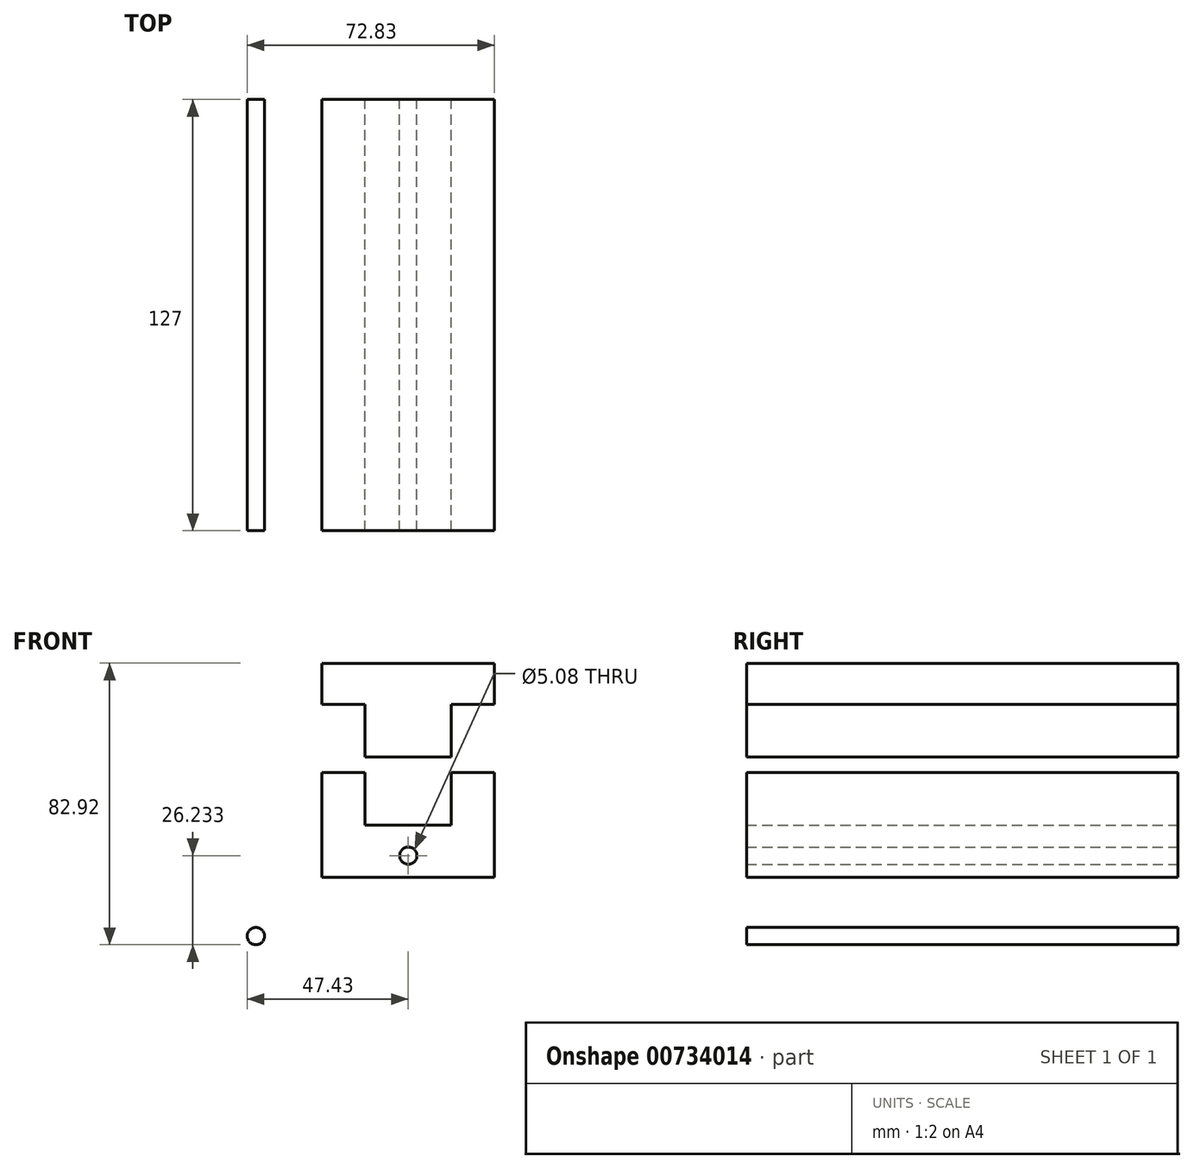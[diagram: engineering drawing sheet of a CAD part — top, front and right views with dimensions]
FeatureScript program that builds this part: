
annotation { "Feature Type Name" : "Feature", "Feature Type Description" : "" }
export const myFeature = defineFeature(function(context is Context, id is Id, definition is map)
    precondition{}
    {
        {
            var Q0;
            Q0=qCreatedBy(makeId("Front.planeOp"),FACE);
            var sketch = newSketch(context, id + "F0", { "sketchPlane" : qUnion([Q0])});
            skLineSegment(sketch, "E0.bottom", {"start": v(-25.4, -15.45) * mm, "end": v(25.4, -15.45) * mm});
            skLineSegment(sketch, "E0.top", {"start": v(-25.4, 15.45) * mm, "end": v(25.4, 15.45) * mm});
            skLineSegment(sketch, "E0.left", {"start": v(-25.4, -15.45) * mm, "end": v(-25.4, 15.45) * mm});
            skLineSegment(sketch, "E0.right", {"start": v(25.4, -15.45) * mm, "end": v(25.4, 15.45) * mm});
            skPoint(sketch, "E0.middle", {"position": v(0, 0) * mm});
            skLineSegment(sketch, "E1", {"start": v(-12.7, 15.45) * mm, "end": v(-12.7, 0) * mm});
            skLineSegment(sketch, "E2", {"start": v(-12.7, 0) * mm, "end": v(12.7, 0) * mm});
            skLineSegment(sketch, "E3", {"start": v(12.7, 0) * mm, "end": v(12.7, 15.45) * mm});
            skCircle(sketch, "E4", {"center": v(0, -9.03) * mm, "radius": 2.54 * mm});
            skSolve(sketch);
        }
        {
            var Q0;
            Q0=makeQuery(id+"F0.imprint","IMPRINT",FACE,{"disambiguationData":[TD([[makeQuery(id+"F0.imprint","IMPRINT",EDGE,{"derivedFrom":sQuery(id+"F0.wireOp",EDGE,"E0.bottom")}),1.0]])]});
            extrude(context, id + "F1", {"entities" : qUnion([Q0]), "endBound" : BoundingType.SYMMETRIC, "depth" : 127 * mm, "offsetDistance" : 25.4 * mm});
        }
        {
            var Q0;
            Q0=qCreatedBy(makeId("Front.planeOp"),FACE);
            var sketch = newSketch(context, id + "F2", { "sketchPlane" : qUnion([Q0])});
            skLineSegment(sketch, "E5.bottom", {"start": v(-12.7, 20.04) * mm, "end": v(12.7, 20.04) * mm});
            skLineSegment(sketch, "E5.top", {"start": v(-12.7, 44.5) * mm, "end": v(12.7, 44.5) * mm});
            skLineSegment(sketch, "E5.left", {"start": v(-12.7, 20.04) * mm, "end": v(-12.7, 44.5) * mm});
            skLineSegment(sketch, "E5.right", {"start": v(12.7, 20.04) * mm, "end": v(12.7, 44.5) * mm});
            skPoint(sketch, "E5.middle", {"position": v(0, 32.27) * mm});
            skLineSegment(sketch, "E6.bottom", {"start": v(-25.4, 35.49) * mm, "end": v(25.4, 35.49) * mm});
            skLineSegment(sketch, "E6.top", {"start": v(-25.4, 47.66) * mm, "end": v(25.4, 47.66) * mm});
            skLineSegment(sketch, "E6.left", {"start": v(-25.4, 35.49) * mm, "end": v(-25.4, 47.66) * mm});
            skLineSegment(sketch, "E6.right", {"start": v(25.4, 35.49) * mm, "end": v(25.4, 47.66) * mm});
            skPoint(sketch, "E6.middle", {"position": v(0, 41.57) * mm});
            skSolve(sketch);
        }
        {
            var Q0;
            Q0 = qSketchRegion(id + "F2", true);
            extrude(context, id + "F3", {"entities" : qUnion([Q0]), "endBound" : BoundingType.SYMMETRIC, "depth" : 127 * mm, "offsetDistance" : 25.4 * mm});
        }
        {
            var Q0;
            Q0=qCreatedBy(makeId("Front.planeOp"),FACE);
            var sketch = newSketch(context, id + "F4", { "sketchPlane" : qUnion([Q0])});
            skCircle(sketch, "E7", {"center": v(-44.9, -32.72) * mm, "radius": 2.54 * mm});
            skSolve(sketch);
        }
        {
            var Q0;
            Q0 = qSketchRegion(id + "F4", true);
            extrude(context, id + "F5", {"entities" : qUnion([Q0]), "endBound" : BoundingType.SYMMETRIC, "depth" : 127 * mm, "offsetDistance" : 25.4 * mm});
        }
    });
